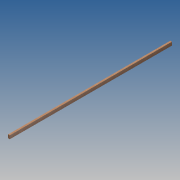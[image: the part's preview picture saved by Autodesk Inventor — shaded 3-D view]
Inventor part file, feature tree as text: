
AUTODESK INVENTOR PART (.ipt)
format: ipt  version: 2013 (Build 170138000, 138)  size: 68,096 bytes
history: native  units: in
note: dims shown in document units (in); Inventor stores cm internally (conversion verified against a paired STEP export)
features: extrude x1, sketch x1
ambient origin geometry x8: Origin, YZ Plane, XZ Plane, XY Plane, X Axis, Y Axis, Z Axis, Center Point
bodies: Solid1 (feature_tree)
feature tree (2):
  extrude  "Extrusion1"  Depth=3.5in
  sketch  "Sketch1"  dims[d0=1.75in d1=3.5in d2=169.0in d3=0.0in]
